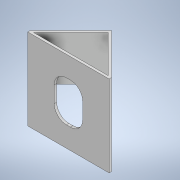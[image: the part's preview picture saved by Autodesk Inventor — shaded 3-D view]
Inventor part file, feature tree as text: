
AUTODESK INVENTOR PART (.ipt)
format: ipt  version: 2020 (Build 240168000, 168)  size: 126,976 bytes
history: native  units: mm
features: extrude x3, sketch x3
ambient origin geometry x8: Origin, YZ Plane, XZ Plane, XY Plane, X Axis, Y Axis, Z Axis, Center Point
bodies: Solid1 (feature_tree)
feature tree (6):
  extrude  "Extrusion1"  Depth=100.0mm
  extrude  "Extrusion2"  TaperAngle=45.0deg  [1 undecoded]
  extrude  "Extrusion3"  Depth=3.0mm
  sketch  "Sketch1"  dims[d0=100.0mm d1=100.0mm]
  sketch  "Sketch2"  dims[d2=3.0mm d3=0.0mm d4=45.0deg]
  sketch  "Sketch3"  dims[d5=3.0mm d6=3.0mm d7=55.0mm d8=0.0mm d9=35.0mm d10=50.0mm d11=15.0mm d12=3.0mm d13=0.0mm]
note: 1 required parameter value undecoded (feature->parameter linkage not recoverable at this tier; creation-order binding heuristic only, values carry confidence <= 0.55)
